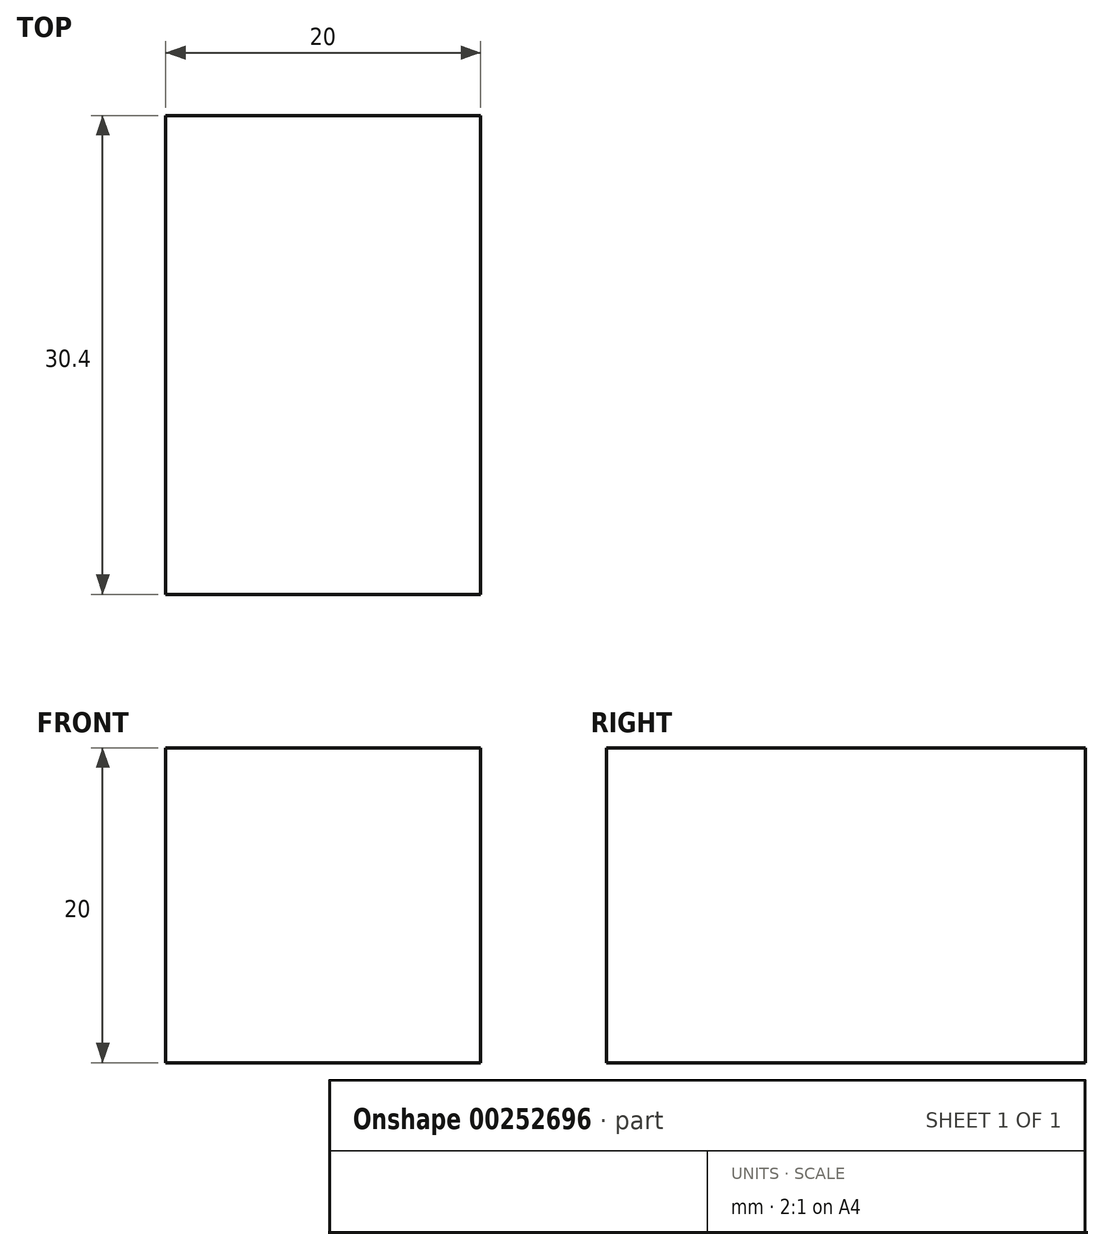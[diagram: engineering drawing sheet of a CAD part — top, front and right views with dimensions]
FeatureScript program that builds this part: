
annotation { "Feature Type Name" : "Feature", "Feature Type Description" : "" }
export const myFeature = defineFeature(function(context is Context, id is Id, definition is map)
    precondition{}
    {
        {
            var Q0;
            Q0=qCreatedBy(makeId("Front.planeOp"),FACE);
            var sketch = newSketch(context, id + "F0", { "sketchPlane" : qUnion([Q0])});
            skLineSegment(sketch, "E0.bottom", {"start": v(0, 0) * mm, "end": v(20, 0) * mm});
            skLineSegment(sketch, "E0.top", {"start": v(0, 20) * mm, "end": v(20, 20) * mm});
            skLineSegment(sketch, "E0.left", {"start": v(0, 0) * mm, "end": v(0, 20) * mm});
            skLineSegment(sketch, "E0.right", {"start": v(20, 0) * mm, "end": v(20, 20) * mm});
            skSolve(sketch);
        }
        {
            var Q0;
            Q0=makeQuery(id+"F0.imprint","IMPRINT",FACE,{"disambiguationData":[TD([[makeQuery(id+"F0.imprint","IMPRINT",EDGE,{"derivedFrom":sQuery(id+"F0.wireOp",EDGE,"E0.bottom")}),1.0]])]});
            extrude(context, id + "F1", {"entities" : qUnion([Q0]), "depth" : 5 * mm});
        }
        {
            var Q0;
            Q0=makeQuery(id+"F1.opExtrude","CAP_FACE",FACE,{"disambiguationData":[OSD([sQuery(id+"F0.wireOp",EDGE,"E0.bottom"),sQuery(id+"F0.wireOp",EDGE,"E0.top"),sQuery(id+"F0.wireOp",EDGE,"E0.left"),sQuery(id+"F0.wireOp",EDGE,"E0.right")])],"isStart":false});
            var sketch = newSketch(context, id + "F2", { "sketchPlane" : qUnion([Q0])});
            skSolve(sketch);
        }
        {
            var Q0;
            Q0=makeQuery(id+"F2.imprint","IMPRINT",FACE,{"disambiguationData":[TD([[makeQuery(id+"F2.imprint","IMPRINT",EDGE,{"derivedFrom":makeQuery(id+"F1.opExtrude","CAP_EDGE",EDGE,{"disambiguationData":[OSD([sQuery(id+"F0.wireOp",EDGE,"E0.bottom")])],"isStart":false})}),1.0]])]});
            extrude(context, id + "F3", {"entities" : qUnion([Q0]), "operationType" : NewBodyOperationType.ADD, "depth" : 25.4 * mm});
        }
    });
